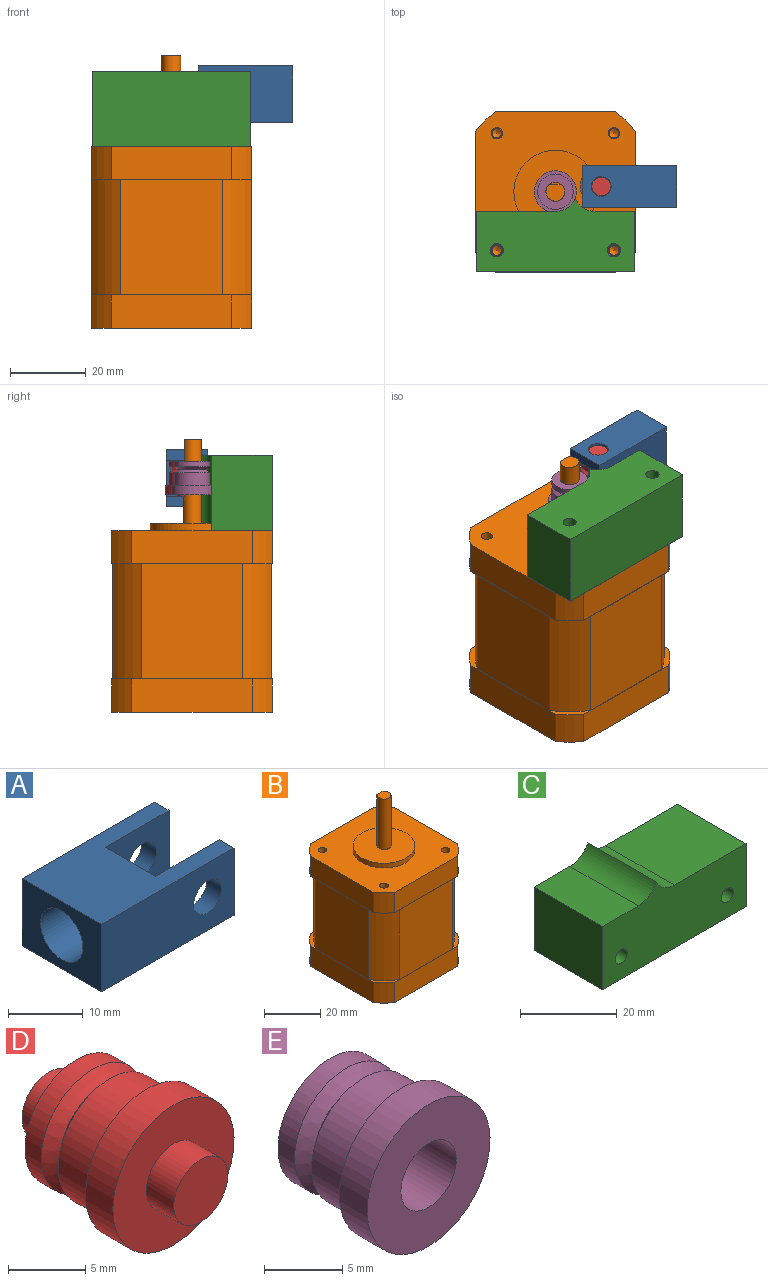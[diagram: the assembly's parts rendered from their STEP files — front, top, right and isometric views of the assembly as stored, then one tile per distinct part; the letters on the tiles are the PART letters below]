
ASSEMBLY  parts=5 mates=6
PART A: 14 faces, bbox 25x15x11 mm
  f0: plane 11x2.75mm, normal (1,0,0), area 30.2mm2, adj f3,f5,f8,f10
  f1: cylinder r=2.62mm len=5.25mm, axis (0,1,0), area 45.4mm2, adj f7,f11
  f2: plane 15x11mm, normal (-1,0,0), area 114.7mm2, adj f3,f5,f7,f8,f12
  f3: plane 25x15mm, normal (0,0,-1), area 261mm2, adj f0,f2,f4,f7,f8,f9,f10,f11
  f4: plane 11x2.75mm, normal (1,0,0), area 30.2mm2, adj f3,f5,f7,f11
  f5: plane 25x15mm, normal (0,0,1), area 261mm2, adj f0,f2,f4,f7,f8,f9,f10,f11
  f6: cylinder r=2.62mm len=5.25mm, axis (0,1,0), area 45.4mm2, adj f8,f10
  f7: plane 25x11mm, normal (0,-1,0), area 253.4mm2, adj f1,f2,f3,f4,f5
  f8: plane 25x11mm, normal (0,1,0), area 253.4mm2, adj f0,f2,f3,f5,f6
  f9: plane 11x9.5mm, normal (1,0,0), area 104.5mm2, adj f3,f5,f10,f11
  f10: plane 12x11mm, normal (0,-1,0), area 110.4mm2, adj f0,f3,f5,f6,f9
  f11: plane 12x11mm, normal (0,1,0), area 110.4mm2, adj f1,f3,f4,f5,f9
  f12: cylinder r=4mm len=8mm, axis (-1,0,0), area 150.8mm2, adj f2,f13
  f13: plane 8x8mm, normal (-1,0,0), area 50.3mm2, adj f12
PART B: 50 faces, bbox 42.4x42.4x72 mm
  f0: cylinder r=2.5mm len=22mm, axis (0,0,-1), area 297.3mm2, adj f1,f2,f29,f30
  f1: plane 5x4.5mm, normal (0,0,1), area 18.6mm2, adj f0,f29
  f2: plane 22x22mm, normal (0,0,1), area 360.5mm2, adj f0,f3
  f3: cylinder r=11mm len=22mm, axis (0,0,-1), area 138.2mm2, adj f2,f8
  f4: plane 31.78x8.75mm, normal (1,0,0), area 278mm2, adj f8,f9,f10,f32
  f5: plane 31.78x8.75mm, normal (0,-1,0), area 278mm2, adj f8,f9,f11,f32
  f6: plane 31.78x8.75mm, normal (-1,0,0), area 278mm2, adj f8,f11,f12,f32
  f7: plane 31.78x8.75mm, normal (0,1,0), area 278mm2, adj f8,f10,f12,f32
  f8: plane 42.42x42.42mm, normal (0,0,1), area 1339.6mm2, adj f3,f4,f5,f6,f7,f9,f10,f11
  f9: cylinder r=26.5mm len=8.75mm, axis (0,0,-1), area 66.1mm2, adj f4,f5,f8,f32
  f10: cylinder r=26.5mm len=8.75mm, axis (0,0,-1), area 66.1mm2, adj f4,f7,f8,f32
  f11: cylinder r=26.5mm len=8.75mm, axis (0,0,-1), area 66.1mm2, adj f5,f6,f8,f32
  f12: cylinder r=26.5mm len=8.75mm, axis (0,0,-1), area 66.1mm2, adj f6,f7,f8,f32
  f13: cone r=1.25mm half-angle=59deg, axis (0,0,1), area 5.7mm2, adj f14
  f14: cylinder r=1.25mm len=2.5mm, axis (0,0,1), area 11.8mm2, adj f13,f15
  f15: plane 3x3mm, normal (0,0,1), area 2.2mm2, adj f14,f16
  f16: cylinder r=1.5mm len=6mm, axis (0,0,1), area 56.5mm2, adj f8,f15
  f17: cone r=1.25mm half-angle=59deg, axis (0,0,1), area 5.7mm2, adj f18
  f18: cylinder r=1.25mm len=2.5mm, axis (0,0,1), area 11.8mm2, adj f17,f19
  f19: plane 3x3mm, normal (0,0,1), area 2.2mm2, adj f18,f20
  f20: cylinder r=1.5mm len=6mm, axis (0,0,1), area 56.5mm2, adj f8,f19
  f21: cone r=1.25mm half-angle=59deg, axis (0,0,1), area 5.7mm2, adj f22
  f22: cylinder r=1.25mm len=2.5mm, axis (0,0,1), area 11.8mm2, adj f21,f23
  f23: plane 3x3mm, normal (0,0,1), area 2.2mm2, adj f22,f24
  f24: cylinder r=1.5mm len=6mm, axis (0,0,1), area 56.5mm2, adj f8,f23
  f25: cone r=1.25mm half-angle=59deg, axis (0,0,1), area 5.7mm2, adj f26
  f26: cylinder r=1.25mm len=2.5mm, axis (0,0,1), area 11.8mm2, adj f25,f27
  f27: plane 3x3mm, normal (0,0,1), area 2.2mm2, adj f26,f28
  f28: cylinder r=1.5mm len=6mm, axis (0,0,1), area 56.5mm2, adj f8,f27
  f29: plane 15x3mm, normal (0,1,0), area 45mm2, adj f0,f1,f30
  f30: plane 3x0.5mm, normal (0,0,1), area 1mm2, adj f0,f29
  f31: plane 42.42x42.42mm, normal (0,0,1), area 67.2mm2, adj f33,f34,f35,f36,f37,f38,f39,f40
  f32: plane 42.42x42.42mm, normal (0,0,-1), area 67.2mm2, adj f4,f5,f6,f7,f9,f10,f11,f12
  f33: cylinder r=25mm len=30.5mm, axis (0,0,1), area 335.5mm2, adj f31,f32,f34,f40
  f34: plane 30.5x26.79mm, normal (0,1,0), area 817.1mm2, adj f31,f32,f33,f35
  f35: cylinder r=25mm len=30.5mm, axis (0,0,1), area 335.5mm2, adj f31,f32,f34,f36
  f36: plane 30.5x26.79mm, normal (1,0,0), area 817.1mm2, adj f31,f32,f35,f37
  f37: cylinder r=25mm len=30.5mm, axis (0,0,1), area 335.5mm2, adj f31,f32,f36,f38
  f38: plane 30.5x26.79mm, normal (0,-1,0), area 817.1mm2, adj f31,f32,f37,f39
  f39: cylinder r=25mm len=30.5mm, axis (0,0,1), area 335.5mm2, adj f31,f32,f38,f40
  f40: plane 30.5x26.79mm, normal (-1,0,0), area 817.1mm2, adj f31,f32,f33,f39
  f41: plane 42.42x42.42mm, normal (0,0,-1), area 1748.1mm2, adj f42,f43,f44,f45,f46,f47,f48,f49
  f42: cylinder r=26.5mm len=8.75mm, axis (0,0,-1), area 66.1mm2, adj f31,f41,f48,f49
  f43: cylinder r=26.5mm len=8.75mm, axis (0,0,-1), area 66.1mm2, adj f31,f41,f47,f48
  f44: cylinder r=26.5mm len=8.75mm, axis (0,0,-1), area 66.1mm2, adj f31,f41,f46,f47
  f45: cylinder r=26.5mm len=8.75mm, axis (0,0,-1), area 66.1mm2, adj f31,f41,f46,f49
  f46: plane 31.78x8.75mm, normal (0,1,0), area 278mm2, adj f31,f41,f44,f45
  f47: plane 31.78x8.75mm, normal (-1,0,0), area 278mm2, adj f31,f41,f43,f44
  f48: plane 31.78x8.75mm, normal (0,-1,0), area 278mm2, adj f31,f41,f42,f43
  f49: plane 31.78x8.75mm, normal (1,0,0), area 278mm2, adj f31,f41,f42,f45
PART C: 11 faces, bbox 42x20x19.4 mm
  f0: plane 42x20mm, normal (0,0,-1), area 840mm2, adj f1,f6,f7,f8
  f1: plane 20x16mm, normal (1,0,0), area 320mm2, adj f0,f2,f7,f8
  f2: plane 21x20mm, normal (0,0,1), area 420mm2, adj f1,f3,f7,f8
  f3: cylinder r=5.75mm len=20mm, axis (0,1,0), area 132.3mm2, adj f2,f4,f7,f8
  f4: cylinder r=5.75mm len=20mm, axis (0,1,0), area 132.3mm2, adj f3,f5,f7,f8
  f5: plane 20x10.5mm, normal (0,0,1), area 210mm2, adj f4,f6,f7,f8
  f6: plane 20x16mm, normal (-1,0,0), area 320mm2, adj f0,f5,f7,f8
  f7: plane 42x19.4mm, normal (0,-1,0), area 662.8mm2, adj f0,f1,f2,f3,f4,f5,f6,f9
  f8: plane 42x19.4mm, normal (0,1,0), area 662.8mm2, adj f0,f1,f2,f3,f4,f5,f6,f9
  f9: cylinder r=1.75mm len=20mm, axis (0,-1,0), area 219.9mm2, adj f7,f8
  f10: cylinder r=1.75mm len=20mm, axis (0,-1,0), area 219.9mm2, adj f7,f8
PART D: 12 faces, bbox 11.1x13.9x11.1 mm
  f0: plane 9.4x9.4mm, normal (0,1,0), area 50.2mm2, adj f7,f10
  f1: plane 11.1x11.1mm, normal (0,-1,0), area 77.5mm2, adj f2,f8
  f2: cylinder r=5.55mm len=11.1mm, axis (0,-1,0), area 87.2mm2, adj f1,f3
  f3: plane 11.1x11.1mm, normal (0,1,0), area 27.4mm2, adj f2,f4
  f4: cylinder r=4.7mm len=9.4mm, axis (0,-1,0), area 99.4mm2, adj f3,f5
  f5: cone r=3.7mm half-angle=52.5deg, axis (0,-1,0), area 33.3mm2, adj f4,f6
  f6: cone r=4.7mm half-angle=52.5deg, axis (0,1,0), area 33.3mm2, adj f5,f7
  f7: cylinder r=4.7mm len=9.4mm, axis (0,-1,0), area 44.3mm2, adj f0,f6
  f8: cylinder r=2.48mm len=4.95mm, axis (0,1,0), area 38.9mm2, adj f1,f9
  f9: plane 4.95x4.95mm, normal (0,-1,0), area 19.2mm2, adj f8
  f10: cylinder r=2.48mm len=4.95mm, axis (0,-1,0), area 38.9mm2, adj f0,f11
  f11: plane 4.95x4.95mm, normal (0,1,0), area 19.2mm2, adj f10
PART E: 9 faces, bbox 11.1x8.9x11.1 mm
  f0: plane 9.4x9.4mm, normal (0,1,0), area 49.8mm2, adj f7,f8
  f1: plane 11.1x11.1mm, normal (0,-1,0), area 77.1mm2, adj f2,f8
  f2: cylinder r=5.55mm len=11.1mm, axis (0,-1,0), area 87.2mm2, adj f1,f3
  f3: plane 11.1x11.1mm, normal (0,1,0), area 27.4mm2, adj f2,f4
  f4: cylinder r=4.7mm len=9.4mm, axis (0,-1,0), area 99.4mm2, adj f3,f5
  f5: cone r=3.7mm half-angle=52.5deg, axis (0,-1,0), area 33.3mm2, adj f4,f6
  f6: cone r=4.7mm half-angle=52.5deg, axis (0,1,0), area 33.3mm2, adj f5,f7
  f7: cylinder r=4.7mm len=9.4mm, axis (0,-1,0), area 44.3mm2, adj f0,f6
  f8: cylinder r=2.5mm len=8.9mm, axis (0,-1,0), area 139.8mm2, adj f0,f1
PLACE A rot(axis=(0,0.71,0.71),180deg) t=(21.34,-16.85,23.62)mm
PLACE B t=(-10.77,-12.73,2.24)mm fixed
PLACE C rot(axis=(0,0.71,0.71),180deg) t=(10.23,-33.93,22.24)mm
PLACE D rot(axis=(0.01,-0.71,-0.71),179.2deg) t=(1.34,-11.35,11.72)mm
PLACE E rot(axis=(1,0,0),90deg) t=(-10.77,-12.73,11.72)mm
MATE parallel D.f2 <-> B.f0  axis (0,0,-1) through (1.34,-11.35,17.58)mm
MATE planar D.f8 <-> E.f8  axis (0,0,1) through (1.34,-11.35,14.22)mm
MATE revolute D.f2 <-> A.f1  axis (0,0,1) through (1.34,-11.35,20.62)mm
MATE parallel C.f5 <-> A.f3  axis (0,1,0) through (4.98,-17.93,12.24)mm
MATE fastened C.f7 <-> B.f8  axis (0,0,-1) through (-10.77,-33.93,2.24)mm
MATE slider E.f8 <-> B.f0  axis (0,0,1) through (-10.77,-12.73,20.62)mm
